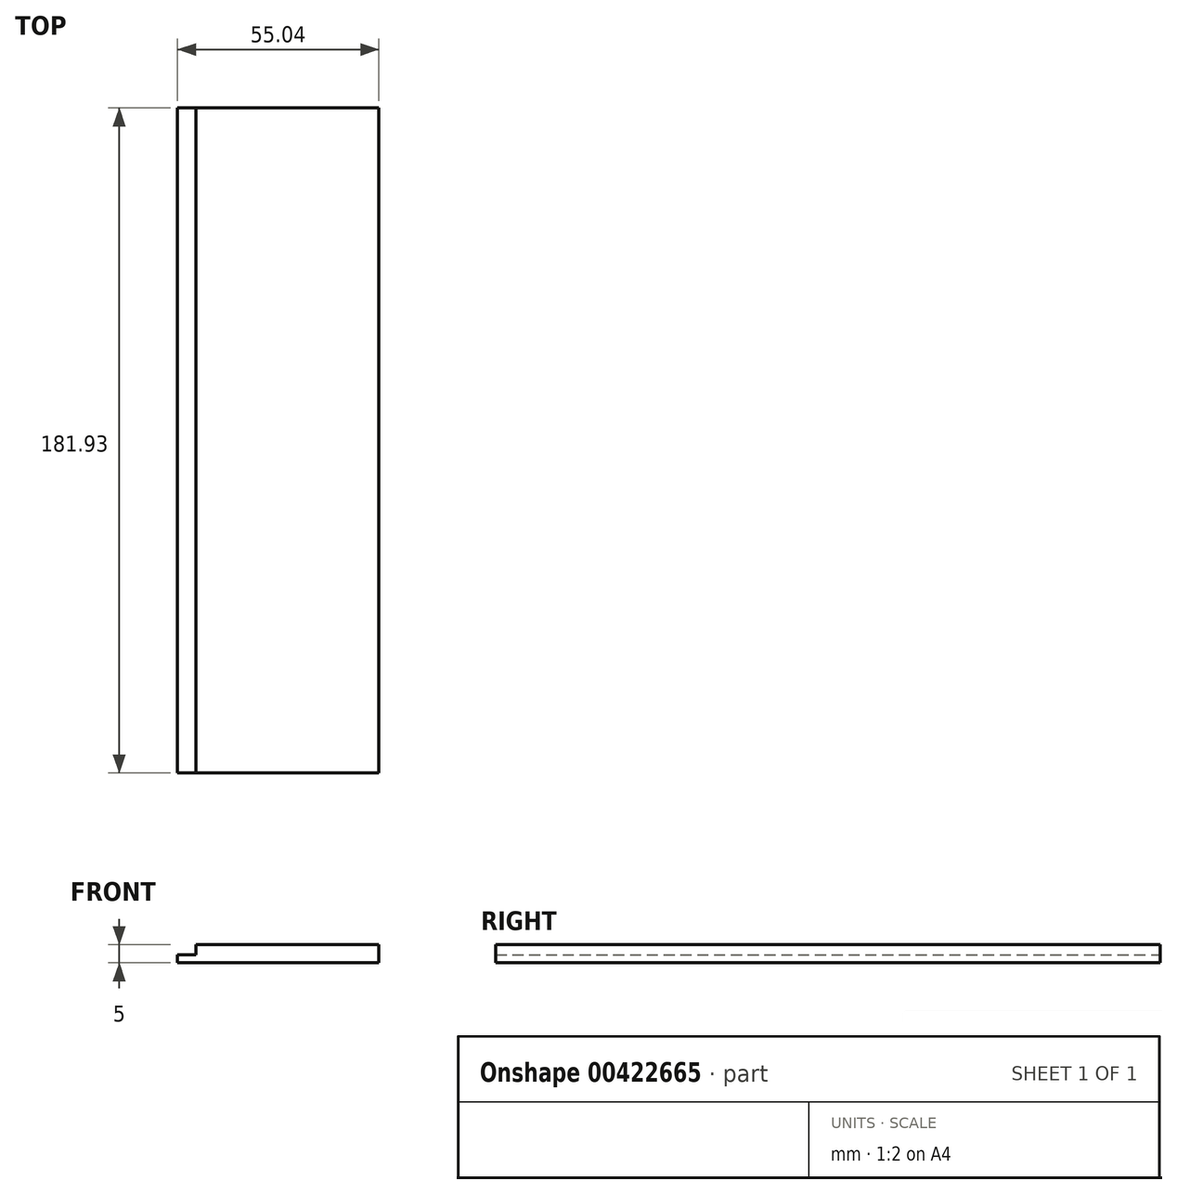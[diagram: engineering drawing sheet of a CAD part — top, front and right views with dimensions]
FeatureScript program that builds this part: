
annotation { "Feature Type Name" : "Feature", "Feature Type Description" : "" }
export const myFeature = defineFeature(function(context is Context, id is Id, definition is map)
    precondition{}
    {
        {
            var Q0;
            Q0=qCreatedBy(makeId("Top.planeOp"),FACE);
            var sketch = newSketch(context, id + "F0", { "sketchPlane" : qUnion([Q0])});
            skLineSegment(sketch, "E0.left", {"start": v(-77.93, 88.2) * mm, "end": v(-77.93, -81.03) * mm});
            skLineSegment(sketch, "E1", {"start": v(-77.93, 88.2) * mm, "end": v(-77.93, 94.55) * mm});
            skLineSegment(sketch, "E2", {"start": v(-77.93, -87.38) * mm, "end": v(-77.93, -81.03) * mm});
            skLineSegment(sketch, "E3", {"start": v(-77.93, 94.55) * mm, "end": v(-22.89, 94.55) * mm});
            skLineSegment(sketch, "E4", {"start": v(-77.93, -87.38) * mm, "end": v(-22.89, -87.38) * mm});
            skLineSegment(sketch, "E5", {"start": v(-22.89, -87.38) * mm, "end": v(-22.89, 94.55) * mm});
            skSolve(sketch);
        }
        {
            var Q0;
            Q0 = qSketchRegion(id + "F0", true);
            extrude(context, id + "F1", {"entities" : qUnion([Q0]), "depth" : 5 * mm});
        }
        {
            var Q0;
            Q0=makeQuery(id+"F1.opExtrude","CAP_FACE",FACE,{"disambiguationData":[OSD([sQuery(id+"F0.wireOp",EDGE,"E0.left"),sQuery(id+"F0.wireOp",EDGE,"E1"),sQuery(id+"F0.wireOp",EDGE,"E2"),sQuery(id+"F0.wireOp",EDGE,"E3"),sQuery(id+"F0.wireOp",EDGE,"E4"),sQuery(id+"F0.wireOp",EDGE,"E5")])],"isStart":false});
            var sketch = newSketch(context, id + "F2", { "sketchPlane" : qUnion([Q0])});
            skLineSegment(sketch, "E6.bottom", {"start": v(-77.93, 94.55) * mm, "end": v(-72.88, 94.55) * mm});
            skLineSegment(sketch, "E6.top", {"start": v(-77.93, -87.38) * mm, "end": v(-72.88, -87.38) * mm});
            skLineSegment(sketch, "E6.left", {"start": v(-77.93, 94.55) * mm, "end": v(-77.93, -87.38) * mm});
            skLineSegment(sketch, "E6.right", {"start": v(-72.88, 94.55) * mm, "end": v(-72.88, -87.38) * mm});
            skSolve(sketch);
        }
        {
            var Q0;
            Q0 = qSketchRegion(id + "F2", true);
            extrude(context, id + "F3", {"entities" : qUnion([Q0]), "operationType" : NewBodyOperationType.REMOVE, "oppositeDirection" : true, "depth" : 2.8 * mm});
        }
    });
